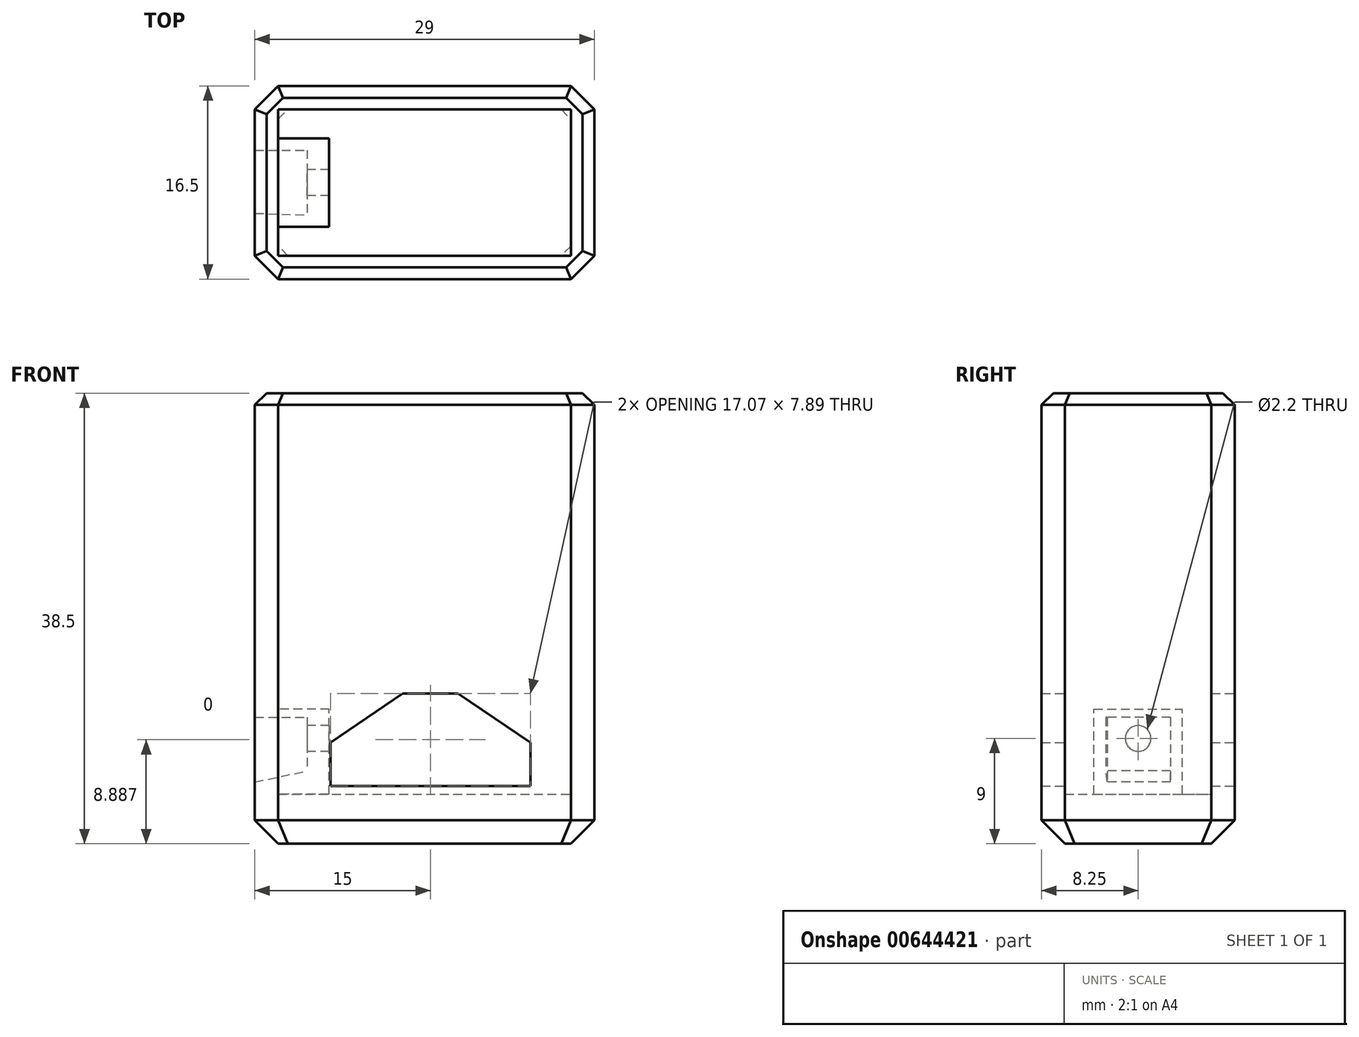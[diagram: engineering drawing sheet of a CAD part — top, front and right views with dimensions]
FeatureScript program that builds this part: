
annotation { "Feature Type Name" : "Feature", "Feature Type Description" : "" }
export const myFeature = defineFeature(function(context is Context, id is Id, definition is map)
    precondition{}
    {
        {
            var Q0;
            Q0=qCreatedBy(makeId("Top.planeOp"),FACE);
            var sketch = newSketch(context, id + "F0", { "sketchPlane" : qUnion([Q0])});
            skLineSegment(sketch, "E0.bottom", {"start": v(0, 0) * mm, "end": v(29, 0) * mm});
            skLineSegment(sketch, "E0.top", {"start": v(0, 16.5) * mm, "end": v(29, 16.5) * mm});
            skLineSegment(sketch, "E0.left", {"start": v(0, 0) * mm, "end": v(0, 16.5) * mm});
            skLineSegment(sketch, "E0.right", {"start": v(29, 0) * mm, "end": v(29, 16.5) * mm});
            skSolve(sketch);
        }
        {
            var Q0;
            Q0 = qSketchRegion(id + "F0", true);
            extrude(context, id + "F1", {"entities" : qUnion([Q0]), "depth" : 38.5 * mm, "offsetDistance" : 25 * mm});
        }
        {
            var Q0;
            Q0=makeQuery(id+"F1.opExtrude","CAP_FACE",FACE,{"disambiguationData":[OSD([sQuery(id+"F0.wireOp",EDGE,"E0.bottom"),sQuery(id+"F0.wireOp",EDGE,"E0.top"),sQuery(id+"F0.wireOp",EDGE,"E0.left"),sQuery(id+"F0.wireOp",EDGE,"E0.right")])],"isStart":false});
            shell(context, id + "F2", {"entities" : qUnion([Q0]), "thickness" : 2 * mm});
        }
        {
            var Q0;
            Q0=makeQuery(id+"F2.opShell","OFFSET_FACE",FACE,{"disambiguationData":[OSD([sQuery(id+"F0.wireOp",EDGE,"E0.bottom"),sQuery(id+"F0.wireOp",EDGE,"E0.top"),sQuery(id+"F0.wireOp",EDGE,"E0.left"),sQuery(id+"F0.wireOp",EDGE,"E0.right")])]});
            extrude(context, id + "F3", {"entities" : qUnion([Q0]), "operationType" : NewBodyOperationType.ADD, "depth" : 2.25 * mm, "offsetDistance" : 25 * mm});
        }
        {
            var Q0;
            Q0=makeQuery(id+"F1.opExtrude","SWEPT_EDGE",EDGE,{"disambiguationData":[OSD([sQuery(id+"F0.wireOp",EDGE,"E0.bottom"),sQuery(id+"F0.wireOp",EDGE,"E0.left")])]});
            var Q1;
            Q1=makeQuery(id+"F1.opExtrude","SWEPT_EDGE",EDGE,{"disambiguationData":[OSD([sQuery(id+"F0.wireOp",EDGE,"E0.top"),sQuery(id+"F0.wireOp",EDGE,"E0.left")])]});
            var Q2;
            Q2=makeQuery(id+"F1.opExtrude","SWEPT_EDGE",EDGE,{"disambiguationData":[OSD([sQuery(id+"F0.wireOp",EDGE,"E0.top"),sQuery(id+"F0.wireOp",EDGE,"E0.right")])]});
            var Q3;
            Q3=makeQuery(id+"F1.opExtrude","SWEPT_EDGE",EDGE,{"disambiguationData":[OSD([sQuery(id+"F0.wireOp",EDGE,"E0.bottom"),sQuery(id+"F0.wireOp",EDGE,"E0.right")])]});
            chamfer(context, id + "F4", {"entities" : qUnion([Q0, Q1, Q2, Q3]), "width" : 2 * mm, "tangentPropagation" : true});
        }
        {
            var Q0;
            Q0=makeQuery(id+"F1.opExtrude","CAP_FACE",FACE,{"disambiguationData":[OSD([sQuery(id+"F0.wireOp",EDGE,"E0.bottom"),sQuery(id+"F0.wireOp",EDGE,"E0.top"),sQuery(id+"F0.wireOp",EDGE,"E0.left"),sQuery(id+"F0.wireOp",EDGE,"E0.right")])],"isStart":true});
            chamfer(context, id + "F5", {"entities" : qUnion([Q0]), "width" : 2 * mm, "tangentPropagation" : true});
        }
        {
            var Q0;
            Q0=makeQuery(id+"F1.opExtrude","CAP_EDGE",EDGE,{"disambiguationData":[OSD([sQuery(id+"F0.wireOp",EDGE,"E0.bottom")])],"isStart":false});
            var Q1;
            {var subQ0=sQuery(id+"F0.wireOp",EDGE,"E0.right");var subQ1=sQuery(id+"F0.wireOp",EDGE,"E0.bottom");Q1=makeQuery(id+"F4.opChamfer","BLEND_EDGE",EDGE,{"blendedFrom":[makeQuery(id+"F1.opExtrude","SWEPT_EDGE",EDGE,{"disambiguationData":[OSD([subQ1,subQ0])]}),makeQuery(id+"F1.opExtrude","CAP_FACE",FACE,{"disambiguationData":[OSD([subQ1,sQuery(id+"F0.wireOp",EDGE,"E0.top"),sQuery(id+"F0.wireOp",EDGE,"E0.left"),subQ0])],"isStart":false})],"blendedInto":[makeQuery(id+"F1.opExtrude","CAP_FACE",FACE,{"disambiguationData":[OSD([subQ1,sQuery(id+"F0.wireOp",EDGE,"E0.top"),sQuery(id+"F0.wireOp",EDGE,"E0.left"),subQ0])],"isStart":false})]});}
            var Q2;
            Q2=makeQuery(id+"F1.opExtrude","CAP_EDGE",EDGE,{"disambiguationData":[OSD([sQuery(id+"F0.wireOp",EDGE,"E0.right")])],"isStart":false});
            var Q3;
            {var subQ0=sQuery(id+"F0.wireOp",EDGE,"E0.right");var subQ1=sQuery(id+"F0.wireOp",EDGE,"E0.top");Q3=makeQuery(id+"F4.opChamfer","BLEND_EDGE",EDGE,{"blendedFrom":[makeQuery(id+"F1.opExtrude","SWEPT_EDGE",EDGE,{"disambiguationData":[OSD([subQ1,subQ0])]}),makeQuery(id+"F1.opExtrude","CAP_FACE",FACE,{"disambiguationData":[OSD([sQuery(id+"F0.wireOp",EDGE,"E0.bottom"),subQ1,sQuery(id+"F0.wireOp",EDGE,"E0.left"),subQ0])],"isStart":false})],"blendedInto":[makeQuery(id+"F1.opExtrude","CAP_FACE",FACE,{"disambiguationData":[OSD([sQuery(id+"F0.wireOp",EDGE,"E0.bottom"),subQ1,sQuery(id+"F0.wireOp",EDGE,"E0.left"),subQ0])],"isStart":false})]});}
            var Q4;
            Q4=makeQuery(id+"F1.opExtrude","CAP_EDGE",EDGE,{"disambiguationData":[OSD([sQuery(id+"F0.wireOp",EDGE,"E0.top")])],"isStart":false});
            var Q5;
            {var subQ0=sQuery(id+"F0.wireOp",EDGE,"E0.left");var subQ1=sQuery(id+"F0.wireOp",EDGE,"E0.top");Q5=makeQuery(id+"F4.opChamfer","BLEND_EDGE",EDGE,{"blendedFrom":[makeQuery(id+"F1.opExtrude","SWEPT_EDGE",EDGE,{"disambiguationData":[OSD([subQ1,subQ0])]}),makeQuery(id+"F1.opExtrude","CAP_FACE",FACE,{"disambiguationData":[OSD([sQuery(id+"F0.wireOp",EDGE,"E0.bottom"),subQ1,subQ0,sQuery(id+"F0.wireOp",EDGE,"E0.right")])],"isStart":false})],"blendedInto":[makeQuery(id+"F1.opExtrude","CAP_FACE",FACE,{"disambiguationData":[OSD([sQuery(id+"F0.wireOp",EDGE,"E0.bottom"),subQ1,subQ0,sQuery(id+"F0.wireOp",EDGE,"E0.right")])],"isStart":false})]});}
            var Q6;
            Q6=makeQuery(id+"F1.opExtrude","CAP_EDGE",EDGE,{"disambiguationData":[OSD([sQuery(id+"F0.wireOp",EDGE,"E0.left")])],"isStart":false});
            var Q7;
            {var subQ0=sQuery(id+"F0.wireOp",EDGE,"E0.left");var subQ1=sQuery(id+"F0.wireOp",EDGE,"E0.bottom");Q7=makeQuery(id+"F4.opChamfer","BLEND_EDGE",EDGE,{"blendedFrom":[makeQuery(id+"F1.opExtrude","SWEPT_EDGE",EDGE,{"disambiguationData":[OSD([subQ1,subQ0])]}),makeQuery(id+"F1.opExtrude","CAP_FACE",FACE,{"disambiguationData":[OSD([subQ1,sQuery(id+"F0.wireOp",EDGE,"E0.top"),subQ0,sQuery(id+"F0.wireOp",EDGE,"E0.right")])],"isStart":false})],"blendedInto":[makeQuery(id+"F1.opExtrude","CAP_FACE",FACE,{"disambiguationData":[OSD([subQ1,sQuery(id+"F0.wireOp",EDGE,"E0.top"),subQ0,sQuery(id+"F0.wireOp",EDGE,"E0.right")])],"isStart":false})]});}
            chamfer(context, id + "F6", {"entities" : qUnion([Q0, Q1, Q2, Q3, Q4, Q5, Q6, Q7]), "width" : 1 * mm, "tangentPropagation" : true});
        }
        {
            var Q0;
            Q0=makeQuery(id+"F1.opExtrude","SWEPT_FACE",FACE,{"disambiguationData":[OSD([sQuery(id+"F0.wireOp",EDGE,"E0.top")])]});
            var sketch = newSketch(context, id + "F7", { "sketchPlane" : qUnion([Q0])});
            skLineSegment(sketch, "E1", {"start": v(-23.54, 4.94) * mm, "end": v(-6.46, 4.94) * mm});
            skLineSegment(sketch, "E2", {"start": v(-6.46, 4.94) * mm, "end": v(-6.46, 8.66) * mm});
            skLineSegment(sketch, "E3", {"start": v(-6.46, 8.66) * mm, "end": v(-12.64, 12.83) * mm});
            skLineSegment(sketch, "E4", {"start": v(-12.64, 12.83) * mm, "end": v(-17.37, 12.83) * mm});
            skLineSegment(sketch, "E5", {"start": v(-17.37, 12.83) * mm, "end": v(-23.54, 8.66) * mm});
            skLineSegment(sketch, "E6", {"start": v(-23.54, 8.66) * mm, "end": v(-23.54, 4.94) * mm});
            skSolve(sketch);
        }
        {
            var Q0;
            Q0=makeQuery(id+"F7.imprint","IMPRINT",FACE,{"disambiguationData":[TD([[makeQuery(id+"F7.imprint","IMPRINT",EDGE,{"derivedFrom":sQuery(id+"F7.wireOp",EDGE,"E1")}),1.0]])]});
            extrude(context, id + "F8", {"entities" : qUnion([Q0]), "operationType" : NewBodyOperationType.REMOVE, "endBound" : BoundingType.THROUGH_ALL, "oppositeDirection" : true, "depth" : 25 * mm, "offsetDistance" : 25 * mm});
        }
        {
            var Q0;
            Q0=qCreatedBy(makeId("Right.planeOp"),FACE);
            var sketch = newSketch(context, id + "F9", { "sketchPlane" : qUnion([Q0])});
            skLineSegment(sketch, "E7.bottom", {"start": v(4.48, 4.25) * mm, "end": v(12.02, 4.25) * mm});
            skLineSegment(sketch, "E7.top", {"start": v(4.48, 11.5) * mm, "end": v(12.02, 11.5) * mm});
            skLineSegment(sketch, "E7.left", {"start": v(4.48, 4.25) * mm, "end": v(4.48, 11.5) * mm});
            skLineSegment(sketch, "E7.right", {"start": v(12.02, 4.25) * mm, "end": v(12.02, 11.5) * mm});
            skCircle(sketch, "E8", {"center": v(8.25, 9) * mm, "radius": 1.1 * mm});
            skSolve(sketch);
        }
        {
            var Q0;
            Q0 = qSketchRegion(id + "F9", true);
            extrude(context, id + "F10", {"entities" : qUnion([Q0]), "operationType" : NewBodyOperationType.ADD, "depth" : 6.35 * mm, "offsetDistance" : 25 * mm});
        }
        {
            var Q0;
            Q0=qCreatedBy(makeId("Right.planeOp"),FACE);
            var sketch = newSketch(context, id + "F11", { "sketchPlane" : qUnion([Q0])});
            skLineSegment(sketch, "E9.bottom", {"start": v(11.02, 10.8) * mm, "end": v(5.62, 10.8) * mm});
            skLineSegment(sketch, "E9.top", {"start": v(11.02, 5.27) * mm, "end": v(5.62, 5.27) * mm});
            skLineSegment(sketch, "E9.left", {"start": v(11.02, 10.8) * mm, "end": v(11.02, 5.27) * mm});
            skLineSegment(sketch, "E9.right", {"start": v(5.62, 10.8) * mm, "end": v(5.62, 5.27) * mm});
            skSolve(sketch);
        }
        {
            var Q0;
            Q0=makeQuery(id+"F1.opExtrude","SWEPT_FACE",FACE,{"disambiguationData":[OSD([sQuery(id+"F0.wireOp",EDGE,"E0.left")])]});
            cPlane(context, id + "F12", {"entities" : qUnion([Q0]), "cplaneType" : CPlaneType.OFFSET, "offset" : 4.45 * mm, "oppositeDirection" : true, "width" : 150 * mm, "height" : 150 * mm});
        }
        {
            var Q0;
            Q0=qCreatedBy(id+"F12.planeOp",FACE);
            var sketch = newSketch(context, id + "F13", { "sketchPlane" : qUnion([Q0])});
            skLineSegment(sketch, "E10.bottom", {"start": v(-11.02, 10.8) * mm, "end": v(-5.48, 10.8) * mm});
            skLineSegment(sketch, "E10.top", {"start": v(-11.02, 6.22) * mm, "end": v(-5.48, 6.22) * mm});
            skLineSegment(sketch, "E10.left", {"start": v(-11.02, 10.8) * mm, "end": v(-11.02, 6.22) * mm});
            skLineSegment(sketch, "E10.right", {"start": v(-5.48, 10.8) * mm, "end": v(-5.48, 6.22) * mm});
            skSolve(sketch);
        }
        {
            var Q1;
            Q1 = qSketchRegion(id + "F11", true);
            var Q2;
            Q2 = qSketchRegion(id + "F13", true);
            loft(context, id + "F14", {"operationType" : NewBodyOperationType.REMOVE, "sheetProfilesArray" : [{ "sheetProfileEntities" : qUnion([Q1]) }, { "sheetProfileEntities" : qUnion([Q2]) }]});
        }
    });
